# Revit family: 1120A_LightHAWK2_Night_Light
name_source: partatom
category: Communication Devices
units: mm (PartAtom-declared; Revit-internal decimal feet)

## family parameters
Cut with Voids When Loaded = No
Host = Face
Maintain Annotation Orientation = No
OmniClass Number = 23.85.80.11.27
OmniClass Title = Lighting Controls
Part Type = Normal
Room Calculation Point = No
Round Connector Dimension = Use Diameter
Shared = Yes

## types (1)
- 1120A_LightHAWK2_Night_Light
    Assembly Code = D5090
    Black = Paint - Carbon Black
    Default Elevation = 48 "
    Description = LightHAWK®2 Night Light PIR Wall Switch Sensor
    Features = Digital passive infrared (PIR) sensor 
IntelliDAPT self-adaptive technology—no manual adjustment required
1 Relay model for single-level switching  
Occupancy (auto-on) and Vacancy (manual-on) operating modes 
Night Light mounted under lens 
 1,000 square-foot, 180° coverage area 
RhinoTuff™ vandal resistant lens 
120/277VAC operation 
 No minimum load requirement
Zero Arc Point Switching 
Five-year limited warranty 
120-277 Vac and 347 Vac models
    Height = 4.5 "
    Manufacturer = NX Lighting Controls
    Model = Wall Switch Occupancy Sensors
    Type Comments = LightHAWK®2 Night Light PIR Wall Switch Sensor
    URL = https://www.currentlighting.com
    Warranty = 5-Years Warranty
    White = Paint -  Matte White
    Width = 2.75 "

## geometry (parser evidence)
native form markers: Sweep x2
no freeform markers — native parametric forms only
